# Revit family: Storage-Teknion-LWBHC_Byward_High_Cabinet-R2022
name_source: partatom
category: Furniture
units: mm (PartAtom-declared; Revit-internal decimal feet)

## family parameters
Always vertical = Yes
Cut with Voids When Loaded = No
OmniClass Number = 23.40.20.00
OmniClass Title = General Furniture and Specialties
Render Appearance Source = Family Geometry
Room Calculation Point = No
Shared = Yes
Work Plane-Based = No

## types (4) — shared parameters
Assembly Code = E2020200
Manufacturer = Teknion
Manufacturer Fax = 416.661.4586
Part Number = LWBHC
Product Documentation Link = https://assets.teknion.com
Product Line = Byward
Product Page URL = https://www.teknion.com
Series = Byward
Sustainability Data = https://www.teknion.com
URL = www.teknion.com
Unit Weight URL = http://www.teknion.com
Warranty = http://www.teknion.com
zero-valued in all types: Default Elevation

## per-type parameters (varying)
| type | CC | CO | Description | Model | OC | OO |
| All Open | No | No | Byward High Cabinet, All Open | LWBHCOO______ | No | Yes |
| All Closed | Yes | No | Byward High Cabinet, All Closed | LWBHCCC______ | No | No |
| Left Open, Right Closed | No | No | Byward High Cabinet, Left Open, Right Closed | LWBHCOC______ | Yes | No |
| Left Closed, Right Open | No | Yes | Byward High Cabinet, Left Closed, Right Open | LWBHCCO______ | No | No |

## geometry (parser evidence)
native form markers: Sweep x13
no freeform markers — native parametric forms only
